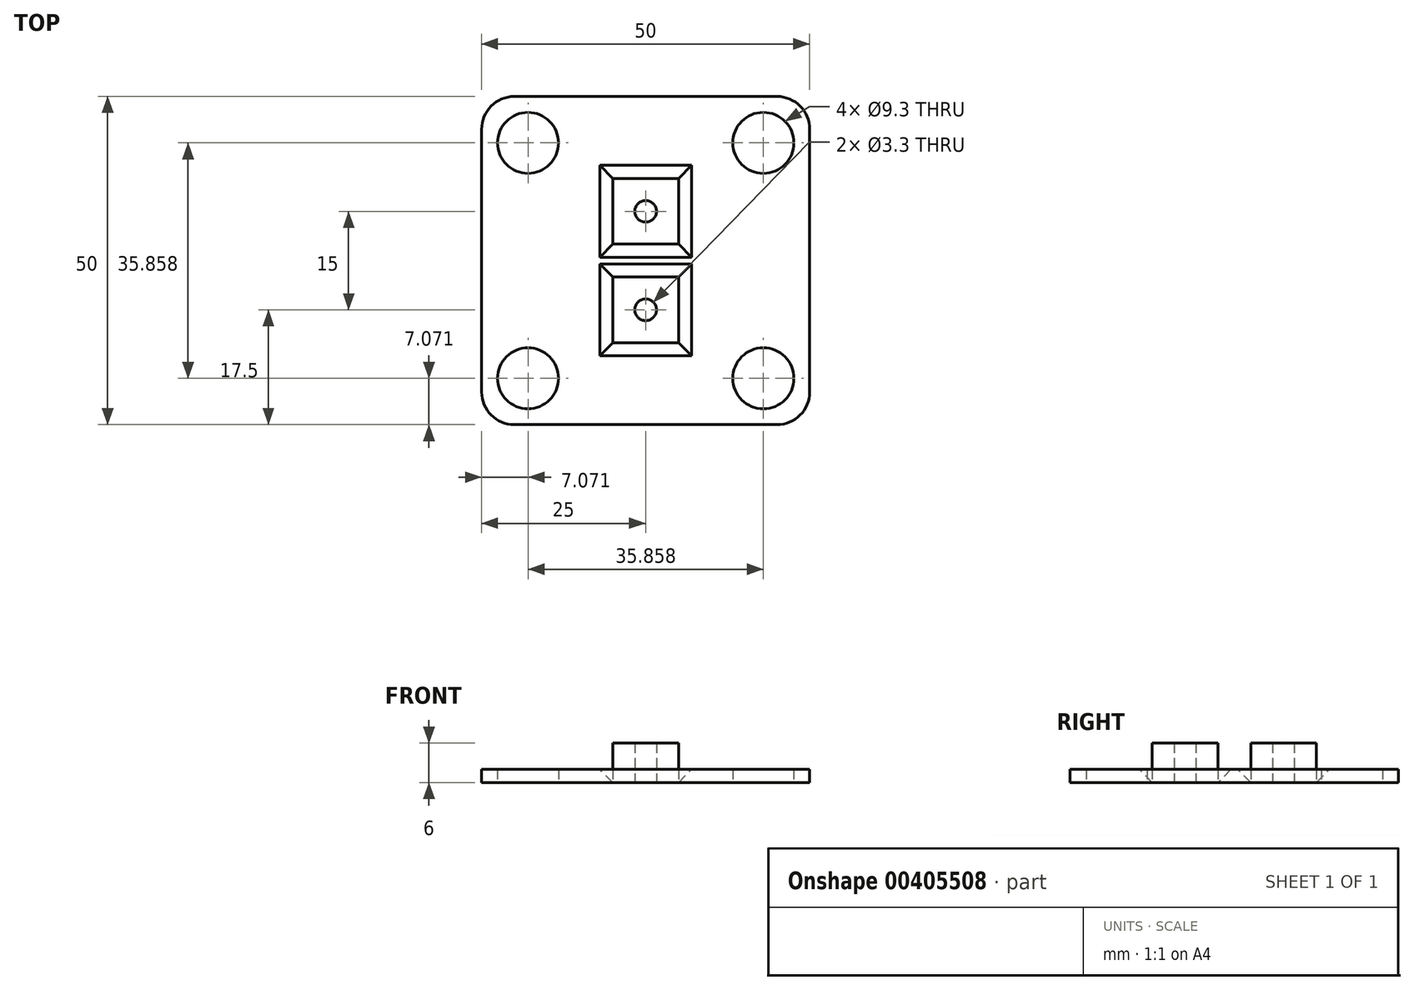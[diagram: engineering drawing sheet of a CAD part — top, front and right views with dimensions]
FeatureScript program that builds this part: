
annotation { "Feature Type Name" : "Feature", "Feature Type Description" : "" }
export const myFeature = defineFeature(function(context is Context, id is Id, definition is map)
    precondition{}
    {
        {
            var Q0;
            Q0=qCreatedBy(makeId("Top.planeOp"),FACE);
            var sketch = newSketch(context, id + "F0", { "sketchPlane" : qUnion([Q0])});
            skLineSegment(sketch, "E0.bottom", {"start": v(-20, 25) * mm, "end": v(20, 25) * mm});
            skLineSegment(sketch, "E0.top", {"start": v(-20, -25) * mm, "end": v(20, -25) * mm});
            skLineSegment(sketch, "E0.left", {"start": v(-25, 20) * mm, "end": v(-25, -20) * mm});
            skLineSegment(sketch, "E0.right", {"start": v(25, 20) * mm, "end": v(25, -20) * mm});
            skLineSegment(sketch, "E1", {"start": v(0, 25) * mm, "end": v(0, -25) * mm, "construction": true});
            skLineSegment(sketch, "E2", {"start": v(-25, 0) * mm, "end": v(25, 0) * mm, "construction": true});
            skLineSegment(sketch, "E3", {"start": v(0, 0) * mm, "end": v(0, 16.75) * mm, "construction": true});
            skLineSegment(sketch, "E4", {"start": v(0, 0) * mm, "end": v(0, -16.75) * mm, "construction": true});
            skLineSegment(sketch, "E5", {"start": v(-25, 25) * mm, "end": v(25, -25) * mm, "construction": true});
            skLineSegment(sketch, "E6", {"start": v(25, 25) * mm, "end": v(-25, -25) * mm, "construction": true});
            skLineSegment(sketch, "E7.bottom", {"start": v(-17.93, 17.93) * mm, "end": v(17.93, 17.93) * mm, "construction": true});
            skLineSegment(sketch, "E7.top", {"start": v(-17.93, -17.93) * mm, "end": v(17.93, -17.93) * mm, "construction": true});
            skLineSegment(sketch, "E7.left", {"start": v(-17.93, 17.93) * mm, "end": v(-17.93, -17.93) * mm, "construction": true});
            skLineSegment(sketch, "E7.right", {"start": v(17.93, 17.93) * mm, "end": v(17.93, -17.93) * mm, "construction": true});
            skCircle(sketch, "E8", {"center": v(-17.93, 17.93) * mm, "radius": 4.65 * mm});
            skCircle(sketch, "E9", {"center": v(17.93, 17.93) * mm, "radius": 4.65 * mm});
            skCircle(sketch, "E10", {"center": v(17.93, -17.93) * mm, "radius": 4.65 * mm});
            skCircle(sketch, "E11", {"center": v(-17.93, -17.93) * mm, "radius": 4.65 * mm});
            skPoint(sketch, "E12.visualSharp", {"position": v(-25, -25) * mm});
            skArc(sketch, "E12.filletArc", {"start": v(-25, -20) * mm, "mid": v(-23.54, -23.54) * mm, "end": v(-20, -25) * mm});
            skPoint(sketch, "E13.visualSharp", {"position": v(-25, 25) * mm});
            skArc(sketch, "E13.filletArc", {"start": v(-20, 25) * mm, "mid": v(-23.54, 23.54) * mm, "end": v(-25, 20) * mm});
            skPoint(sketch, "E14.visualSharp", {"position": v(25, 25) * mm});
            skArc(sketch, "E14.filletArc", {"start": v(25, 20) * mm, "mid": v(23.54, 23.54) * mm, "end": v(20, 25) * mm});
            skPoint(sketch, "E15.visualSharp", {"position": v(25, -25) * mm});
            skArc(sketch, "E15.filletArc", {"start": v(20, -25) * mm, "mid": v(23.54, -23.54) * mm, "end": v(25, -20) * mm});
            skCircle(sketch, "E16", {"center": v(0, 0) * mm, "radius": 7.5 * mm, "construction": true});
            skLineSegment(sketch, "E17", {"start": v(25, 7.5) * mm, "end": v(-25, 7.5) * mm, "construction": true});
            skLineSegment(sketch, "E18", {"start": v(25, -7.5) * mm, "end": v(-25, -7.5) * mm, "construction": true});
            skCircle(sketch, "E19", {"center": v(0, 7.5) * mm, "radius": 1.65 * mm});
            skCircle(sketch, "E20", {"center": v(0, -7.5) * mm, "radius": 1.65 * mm});
            skLineSegment(sketch, "E21", {"start": v(25, -12.5) * mm, "end": v(-25, -12.5) * mm, "construction": true});
            skLineSegment(sketch, "E22", {"start": v(25, -2.5) * mm, "end": v(-25, -2.5) * mm, "construction": true});
            skLineSegment(sketch, "E23", {"start": v(25, 2.5) * mm, "end": v(-25, 2.5) * mm, "construction": true});
            skLineSegment(sketch, "E24", {"start": v(25, 12.5) * mm, "end": v(-25, 12.5) * mm, "construction": true});
            skLineSegment(sketch, "E25", {"start": v(-5, 25) * mm, "end": v(-5, -25) * mm, "construction": true});
            skLineSegment(sketch, "E26", {"start": v(5, 25) * mm, "end": v(5, -25) * mm, "construction": true});
            skLineSegment(sketch, "E27", {"start": v(-5, 12.5) * mm, "end": v(5, 12.5) * mm});
            skLineSegment(sketch, "E28", {"start": v(5, 12.5) * mm, "end": v(5, 2.5) * mm});
            skLineSegment(sketch, "E29", {"start": v(5, 2.5) * mm, "end": v(-5, 2.5) * mm});
            skLineSegment(sketch, "E30", {"start": v(-5, 2.5) * mm, "end": v(-5, 12.5) * mm});
            skLineSegment(sketch, "E31", {"start": v(5, -12.5) * mm, "end": v(5, -2.5) * mm});
            skPoint(sketch, "E31.endSnap0", {"position": v(0, -2.5) * mm});
            skLineSegment(sketch, "E32", {"start": v(5, -2.5) * mm, "end": v(-5, -2.5) * mm});
            skLineSegment(sketch, "E33", {"start": v(-5, -2.5) * mm, "end": v(-5, -12.5) * mm});
            skLineSegment(sketch, "E34", {"start": v(-5, -12.5) * mm, "end": v(5, -12.5) * mm});
            skSolve(sketch);
        }
        {
            var Q0;
            Q0=makeQuery(id+"F0.imprint","IMPRINT",FACE,{"disambiguationData":[TD([[makeQuery(id+"F0.imprint","IMPRINT",EDGE,{"derivedFrom":sQuery(id+"F0.wireOp",EDGE,"E19")}),-1.0]])]});
            var Q1;
            Q1=makeQuery(id+"F0.imprint","IMPRINT",FACE,{"disambiguationData":[TD([[makeQuery(id+"F0.imprint","IMPRINT",EDGE,{"derivedFrom":sQuery(id+"F0.wireOp",EDGE,"E20")}),-1.0]])]});
            extrude(context, id + "F1", {"entities" : qUnion([Q0, Q1]), "depth" : 6 * mm});
        }
        {
            var Q0;
            Q0=makeQuery(id+"F0.imprint","IMPRINT",FACE,{"disambiguationData":[TD([[makeQuery(id+"F0.imprint","IMPRINT",EDGE,{"derivedFrom":sQuery(id+"F0.wireOp",EDGE,"E0.bottom")}),-1.0]])]});
            extrude(context, id + "F2", {"entities" : qUnion([Q0]), "depth" : 2 * mm});
        }
        {
            var Q0;
            Q0=makeQuery(id+"F2.opExtrude","CAP_EDGE",EDGE,{"disambiguationData":[OSD([sQuery(id+"F0.wireOp",EDGE,"E34")])],"isStart":false});
            var Q1;
            Q1=makeQuery(id+"F2.opExtrude","CAP_EDGE",EDGE,{"disambiguationData":[OSD([sQuery(id+"F0.wireOp",EDGE,"E31")])],"isStart":false});
            var Q2;
            Q2=makeQuery(id+"F2.opExtrude","CAP_EDGE",EDGE,{"disambiguationData":[OSD([sQuery(id+"F0.wireOp",EDGE,"E28")])],"isStart":false});
            var Q3;
            Q3=makeQuery(id+"F2.opExtrude","CAP_EDGE",EDGE,{"disambiguationData":[OSD([sQuery(id+"F0.wireOp",EDGE,"E29")])],"isStart":false});
            var Q4;
            Q4=makeQuery(id+"F2.opExtrude","CAP_EDGE",EDGE,{"disambiguationData":[OSD([sQuery(id+"F0.wireOp",EDGE,"E32")])],"isStart":false});
            var Q5;
            Q5=makeQuery(id+"F2.opExtrude","CAP_EDGE",EDGE,{"disambiguationData":[OSD([sQuery(id+"F0.wireOp",EDGE,"E27")])],"isStart":false});
            var Q6;
            Q6=makeQuery(id+"F2.opExtrude","CAP_EDGE",EDGE,{"disambiguationData":[OSD([sQuery(id+"F0.wireOp",EDGE,"E30")])],"isStart":false});
            var Q7;
            Q7=makeQuery(id+"F2.opExtrude","CAP_EDGE",EDGE,{"disambiguationData":[OSD([sQuery(id+"F0.wireOp",EDGE,"E33")])],"isStart":false});
            chamfer(context, id + "F3", {"entities" : qUnion([Q0, Q1, Q2, Q3, Q4, Q5, Q6, Q7]), "width" : 2 * mm, "tangentPropagation" : true});
        }
    });
